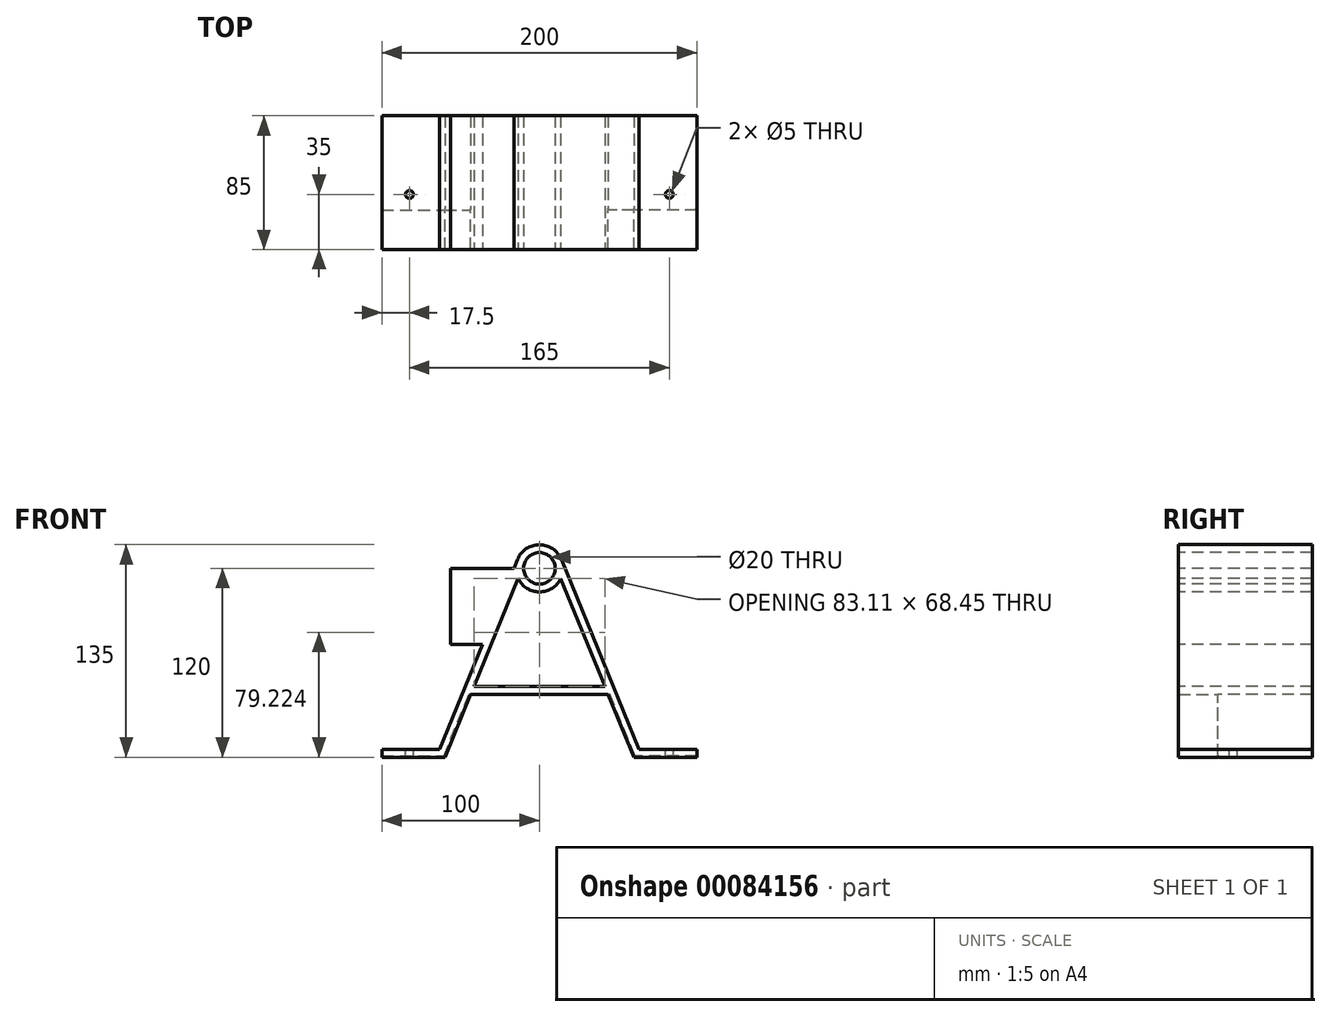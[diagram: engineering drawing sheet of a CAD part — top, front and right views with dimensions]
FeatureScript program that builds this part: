
annotation { "Feature Type Name" : "Feature", "Feature Type Description" : "" }
export const myFeature = defineFeature(function(context is Context, id is Id, definition is map)
    precondition{}
    {
        {
            var Q0;
            Q0=qCreatedBy(makeId("Front.planeOp"),FACE);
            var sketch = newSketch(context, id + "F0", { "sketchPlane" : qUnion([Q0])});
            skArc(sketch, "E0", {"start": v(86.5, 108.45) * mm, "mid": v(100, 100) * mm, "end": v(113.5, 108.45) * mm});
            skLineSegment(sketch, "E1", {"start": v(0, 0) * mm, "end": v(36.65, 0) * mm});
            skLineSegment(sketch, "E2", {"start": v(36.65, 0) * mm, "end": v(86.12, 120.69) * mm});
            skLineSegment(sketch, "E3", {"start": v(0, 0) * mm, "end": v(0, -5) * mm});
            skLineSegment(sketch, "E4", {"start": v(0, -5) * mm, "end": v(40, -5) * mm});
            skLineSegment(sketch, "E5", {"start": v(40, -5) * mm, "end": v(56.4, 35) * mm});
            skLineSegment(sketch, "E6", {"start": v(100, 115) * mm, "end": v(100, -58.47) * mm, "construction": true});
            skLineSegment(sketch, "E7.MirrorCS", {"start": v(160, -5) * mm, "end": v(143.6, 35) * mm});
            skLineSegment(sketch, "E8.MirrorCS", {"start": v(163.35, 0) * mm, "end": v(113.88, 120.69) * mm});
            skLineSegment(sketch, "E9.MirrorCS", {"start": v(200, 0) * mm, "end": v(163.35, 0) * mm});
            skLineSegment(sketch, "E10.MirrorCS", {"start": v(200, -5) * mm, "end": v(160, -5) * mm});
            skLineSegment(sketch, "E11.MirrorCS", {"start": v(200, 0) * mm, "end": v(200, -5) * mm});
            skCircle(sketch, "E12", {"center": v(100, 115) * mm, "radius": 10 * mm});
            skLineSegment(sketch, "E13", {"start": v(58.45, 40) * mm, "end": v(141.55, 40) * mm});
            skLineSegment(sketch, "E14", {"start": v(56.4, 35) * mm, "end": v(143.6, 35) * mm});
            skLineSegment(sketch, "E15.trimOffspring", {"start": v(58.45, 40) * mm, "end": v(86.5, 108.45) * mm});
            skLineSegment(sketch, "E16.trimOffspring", {"start": v(141.55, 40) * mm, "end": v(113.5, 108.45) * mm});
            skArc(sketch, "E17.trimOffspring", {"start": v(113.88, 120.69) * mm, "mid": v(100, 130) * mm, "end": v(86.12, 120.69) * mm});
            skLineSegment(sketch, "E18.bottom", {"start": v(100, 115) * mm, "end": v(43.61, 115) * mm});
            skLineSegment(sketch, "E18.top", {"start": v(100, 66.68) * mm, "end": v(43.61, 66.68) * mm});
            skLineSegment(sketch, "E18.left", {"start": v(100, 115) * mm, "end": v(100, 66.68) * mm});
            skLineSegment(sketch, "E18.right", {"start": v(43.61, 115) * mm, "end": v(43.61, 66.68) * mm});
            skSolve(sketch);
        }
        {
            var Q0;
            Q0=qSketchRegion(id+"F0",true);
            extrude(context, id + "F1", {"entities" : qUnion([Q0]), "oppositeDirection" : true, "depth" : 60 * mm});
        }
        {
            var Q0;
            Q0=makeQuery(id+"F1.opExtrude","SWEPT_FACE",FACE,{"disambiguationData":[OSD([sQuery(id+"F0.wireOp",EDGE,"E9.MirrorCS")])]});
            var sketch = newSketch(context, id + "F2", { "sketchPlane" : qUnion([Q0])});
            skCircle(sketch, "E19", {"center": v(182.5, 10) * mm, "radius": 2.5 * mm});
            skCircle(sketch, "E20", {"center": v(182.5, 42.5) * mm, "radius": 2.5 * mm});
            skLineSegment(sketch, "E21", {"start": v(100, 0) * mm, "end": v(100, 124.34) * mm, "construction": true});
            skCircle(sketch, "E22.MirrorC", {"center": v(17.5, 10) * mm, "radius": 2.5 * mm});
            skCircle(sketch, "E23.MirrorC", {"center": v(17.5, 42.5) * mm, "radius": 2.5 * mm});
            skSolve(sketch);
        }
        {
            var Q0;
            Q0=qSketchRegion(id+"F2",true);
            extrude(context, id + "F3", {"entities" : qUnion([Q0]), "operationType" : NewBodyOperationType.REMOVE, "endBound" : BoundingType.THROUGH_ALL, "oppositeDirection" : true, "depth" : 25 * mm});
        }
        {
            var Q0;
            Q0=makeQuery(id+"F1.opExtrude","SWEPT_EDGE",EDGE,{"disambiguationData":[OSD([sQuery(id+"F0.wireOp",EDGE,"E9.MirrorCS"),sQuery(id+"F0.wireOp",EDGE,"E11.MirrorCS")])]});
            var Q1;
            Q1=makeQuery(id+"F1.opExtrude","SWEPT_EDGE",EDGE,{"disambiguationData":[OSD([sQuery(id+"F0.wireOp",EDGE,"E10.MirrorCS"),sQuery(id+"F0.wireOp",EDGE,"E11.MirrorCS")])]});
            var Q2;
            Q2=makeQuery(id+"F1.opExtrude","SWEPT_EDGE",EDGE,{"disambiguationData":[OSD([sQuery(id+"F0.wireOp",EDGE,"E1"),sQuery(id+"F0.wireOp",EDGE,"E3")])]});
            var Q3;
            Q3=makeQuery(id+"F1.opExtrude","SWEPT_EDGE",EDGE,{"disambiguationData":[OSD([sQuery(id+"F0.wireOp",EDGE,"E3"),sQuery(id+"F0.wireOp",EDGE,"E4")])]});
            var Q4;
            Q4=makeQuery(id+"F1.opExtrude","CAP_EDGE",EDGE,{"disambiguationData":[OSD([sQuery(id+"F0.wireOp",EDGE,"E7.MirrorCS")])],"isStart":true});
            var Q5;
            Q5=makeQuery(id+"F1.opExtrude","CAP_EDGE",EDGE,{"disambiguationData":[OSD([sQuery(id+"F0.wireOp",EDGE,"E10.MirrorCS")])],"isStart":true});
            var Q6;
            Q6=makeQuery(id+"F1.opExtrude","CAP_EDGE",EDGE,{"disambiguationData":[OSD([sQuery(id+"F0.wireOp",EDGE,"E4")])],"isStart":true});
            var Q7;
            Q7=makeQuery(id+"F1.opExtrude","CAP_EDGE",EDGE,{"disambiguationData":[OSD([sQuery(id+"F0.wireOp",EDGE,"E5")])],"isStart":true});
            fillet(context, id + "F4", {"entities" : qUnion([Q0, Q1, Q2, Q3, Q4, Q5, Q6, Q7]), "radius" : 1 * mm, "tangentPropagation" : true, "allowEdgeOverflow" : false});
        }
        {
            var Q0;
            Q0 = qSketchRegion(id + "F0", true);
            var Q1;
            Q1=makeQuery(id+"F1.opExtrude","CAP_FACE",FACE,{"disambiguationData":[OSD([sQuery(id+"F0.wireOp",EDGE,"E0"),sQuery(id+"F0.wireOp",EDGE,"E1"),sQuery(id+"F0.wireOp",EDGE,"E2"),sQuery(id+"F0.wireOp",EDGE,"E3"),sQuery(id+"F0.wireOp",EDGE,"E4"),sQuery(id+"F0.wireOp",EDGE,"E5"),sQuery(id+"F0.wireOp",EDGE,"E7.MirrorCS"),sQuery(id+"F0.wireOp",EDGE,"E8.MirrorCS"),sQuery(id+"F0.wireOp",EDGE,"E9.MirrorCS"),sQuery(id+"F0.wireOp",EDGE,"E10.MirrorCS"),sQuery(id+"F0.wireOp",EDGE,"E11.MirrorCS"),sQuery(id+"F0.wireOp",EDGE,"E12"),sQuery(id+"F0.wireOp",EDGE,"E13"),sQuery(id+"F0.wireOp",EDGE,"E14"),sQuery(id+"F0.wireOp",EDGE,"E15.trimOffspring"),sQuery(id+"F0.wireOp",EDGE,"E16.trimOffspring"),sQuery(id+"F0.wireOp",EDGE,"E17.trimOffspring"),sQuery(id+"F0.wireOp",EDGE,"E18.bottom"),sQuery(id+"F0.wireOp",EDGE,"E18.top"),sQuery(id+"F0.wireOp",EDGE,"E18.right")])],"isStart":false});
            extrude(context, id + "F5", {"entities" : qUnion([Q0, Q1]), "operationType" : NewBodyOperationType.ADD, "depth" : 25 * mm});
        }
    });
